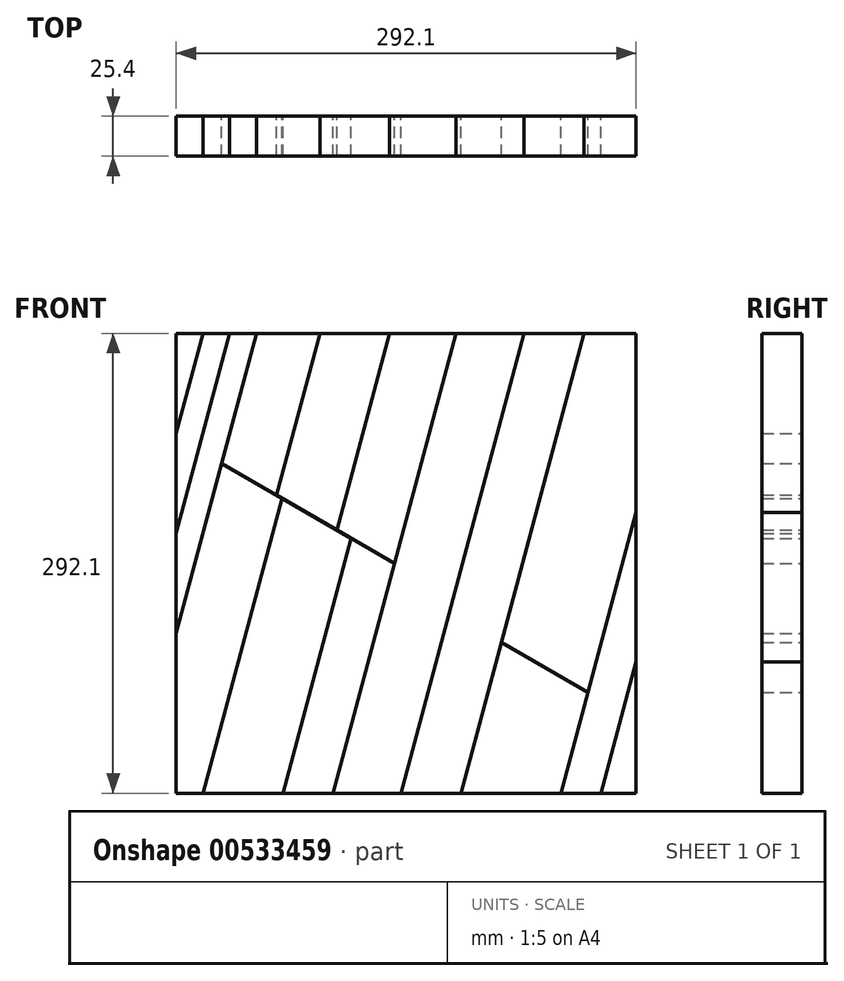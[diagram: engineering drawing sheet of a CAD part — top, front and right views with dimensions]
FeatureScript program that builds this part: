
annotation { "Feature Type Name" : "Feature", "Feature Type Description" : "" }
export const myFeature = defineFeature(function(context is Context, id is Id, definition is map)
    precondition{}
    {
        {
            var Q0;
            Q0=qCreatedBy(makeId("Front.planeOp"),FACE);
            var sketch = newSketch(context, id + "F0", { "sketchPlane" : qUnion([Q0])});
            skLineSegment(sketch, "E0.bottom", {"start": v(-146.05, -146.05) * mm, "end": v(146.05, -146.05) * mm});
            skLineSegment(sketch, "E0.top", {"start": v(-146.05, 146.05) * mm, "end": v(146.05, 146.05) * mm});
            skLineSegment(sketch, "E0.left", {"start": v(-146.05, -146.05) * mm, "end": v(-146.05, 146.05) * mm});
            skLineSegment(sketch, "E0.right", {"start": v(146.05, -146.05) * mm, "end": v(146.05, 146.05) * mm});
            skPoint(sketch, "E0.middle", {"position": v(0, 0) * mm});
            skSolve(sketch);
        }
        {
            var Q0;
            Q0=makeQuery(id+"F0.imprint","IMPRINT",FACE,{"disambiguationData":[TD([[makeQuery(id+"F0.imprint","IMPRINT",EDGE,{"derivedFrom":sQuery(id+"F0.wireOp",EDGE,"E0.bottom")}),1.0]])]});
            var sketch = newSketch(context, id + "F1", { "sketchPlane" : qUnion([Q0])});
            skLineSegment(sketch, "E1.0", {"start": v(-146.05, -146.05) * mm, "end": v(-146.05, 146.05) * mm});
            skLineSegment(sketch, "E2.0", {"start": v(-146.05, 146.05) * mm, "end": v(146.05, 146.05) * mm});
            skLineSegment(sketch, "E3.0", {"start": v(146.05, -146.05) * mm, "end": v(146.05, 146.05) * mm});
            skLineSegment(sketch, "E4.0", {"start": v(-146.05, -146.05) * mm, "end": v(146.05, -146.05) * mm});
            skLineSegment(sketch, "E5", {"start": v(-146.05, 82.55) * mm, "end": v(-129.04, 146.05) * mm});
            skLineSegment(sketch, "E6", {"start": v(-146.05, 19.05) * mm, "end": v(-112.02, 146.05) * mm});
            skLineSegment(sketch, "E7", {"start": v(-146.05, -44.45) * mm, "end": v(-95, 146.05) * mm});
            skLineSegment(sketch, "E8", {"start": v(-117.37, 63.5) * mm, "end": v(-7.38, 0) * mm});
            skLineSegment(sketch, "E9", {"start": v(31.75, 146.05) * mm, "end": v(-46.52, -146.05) * mm});
            skLineSegment(sketch, "E10", {"start": v(-129.07, -146.05) * mm, "end": v(-78.87, 41.27) * mm});
            skLineSegment(sketch, "E11", {"start": v(-78.27, -146.05) * mm, "end": v(-34.88, 15.87) * mm});
            skLineSegment(sketch, "E12", {"start": v(-3.34, -146.05) * mm, "end": v(74.93, 146.05) * mm});
            skLineSegment(sketch, "E13", {"start": v(34.76, -146.05) * mm, "end": v(113.03, 146.05) * mm});
            skLineSegment(sketch, "E14", {"start": v(98.26, -146.05) * mm, "end": v(146.05, 32.3) * mm});
            skLineSegment(sketch, "E15", {"start": v(60.4, -50.34) * mm, "end": v(115.4, -82.1) * mm});
            skPoint(sketch, "E16.orphan", {"position": v(0, 146.05) * mm});
            skLineSegment(sketch, "E17", {"start": v(123.66, -146.05) * mm, "end": v(146.05, -62.5) * mm});
            skLineSegment(sketch, "E18", {"start": v(-44.03, 21.16) * mm, "end": v(-10.57, 146.05) * mm});
            skLineSegment(sketch, "E19", {"start": v(-82.3, 43.25) * mm, "end": v(-54.75, 146.05) * mm});
            skSolve(sketch);
        }
        {
            var Q0;
            {var subQ6=sQuery(id+"F1.wireOp",EDGE,"E17");Q0=makeQuery(id+"F1.imprint","IMPRINT",FACE,{"disambiguationData":[TD([[makeQuery(id+"F1.imprint","IMPRINT",EDGE,{"derivedFrom":subQ6}),1.0]])]});}
            extrude(context, id + "F2", {"entities" : qUnion([Q0]), "depth" : 25.4 * mm, "offsetDistance" : 25.4 * mm});
        }
        {
            var Q0;
            {var subQ3=sQuery(id+"F1.wireOp",EDGE,"E17");Q0=makeQuery(id+"F1.imprint","IMPRINT",FACE,{"disambiguationData":[TD([[makeQuery(id+"F1.imprint","IMPRINT",EDGE,{"derivedFrom":subQ3}),-1.0]])]});}
            extrude(context, id + "F3", {"entities" : qUnion([Q0]), "depth" : 25.4 * mm, "offsetDistance" : 25.4 * mm});
        }
        {
            var Q0;
            {var subQ5=sQuery(id+"F1.wireOp",EDGE,"E15");Q0=makeQuery(id+"F1.imprint","IMPRINT",FACE,{"disambiguationData":[TD([[makeQuery(id+"F1.imprint","IMPRINT",EDGE,{"derivedFrom":subQ5}),-1.0]])]});}
            extrude(context, id + "F4", {"entities" : qUnion([Q0]), "depth" : 25.4 * mm, "offsetDistance" : 25.4 * mm});
        }
        {
            var Q0;
            {var subQ3=sQuery(id+"F1.wireOp",EDGE,"E15");Q0=makeQuery(id+"F1.imprint","IMPRINT",FACE,{"disambiguationData":[TD([[makeQuery(id+"F1.imprint","IMPRINT",EDGE,{"derivedFrom":subQ3}),1.0]])]});}
            extrude(context, id + "F5", {"entities" : qUnion([Q0]), "depth" : 25.4 * mm, "offsetDistance" : 25.4 * mm});
        }
        {
            var Q0;
            {var subQ4=sQuery(id+"F1.wireOp",EDGE,"E12");Q0=makeQuery(id+"F1.imprint","IMPRINT",FACE,{"disambiguationData":[TD([[makeQuery(id+"F1.imprint","IMPRINT",EDGE,{"derivedFrom":subQ4}),-1.0]])]});}
            extrude(context, id + "F6", {"entities" : qUnion([Q0]), "depth" : 25.4 * mm, "offsetDistance" : 25.4 * mm});
        }
        {
            var Q0;
            {var subQ6=sQuery(id+"F1.wireOp",EDGE,"E12");Q0=makeQuery(id+"F1.imprint","IMPRINT",FACE,{"disambiguationData":[TD([[makeQuery(id+"F1.imprint","IMPRINT",EDGE,{"derivedFrom":subQ6}),1.0]])]});}
            extrude(context, id + "F7", {"entities" : qUnion([Q0]), "depth" : 25.4 * mm, "offsetDistance" : 25.4 * mm});
        }
        {
            var Q0;
            {var subQ3=sQuery(id+"F1.wireOp",EDGE,"E11");Q0=makeQuery(id+"F1.imprint","IMPRINT",FACE,{"disambiguationData":[TD([[makeQuery(id+"F1.imprint","IMPRINT",EDGE,{"derivedFrom":subQ3}),-1.0]])]});}
            extrude(context, id + "F8", {"entities" : qUnion([Q0]), "depth" : 25.4 * mm, "offsetDistance" : 25.4 * mm});
        }
        {
            var Q0;
            {var subQ5=sQuery(id+"F1.wireOp",EDGE,"E18");Q0=makeQuery(id+"F1.imprint","IMPRINT",FACE,{"disambiguationData":[TD([[makeQuery(id+"F1.imprint","IMPRINT",EDGE,{"derivedFrom":subQ5}),-1.0]])]});}
            extrude(context, id + "F9", {"entities" : qUnion([Q0]), "depth" : 25.4 * mm, "offsetDistance" : 25.4 * mm});
        }
        {
            var Q0;
            {var subQ2=sQuery(id+"F1.wireOp",EDGE,"E18");Q0=makeQuery(id+"F1.imprint","IMPRINT",FACE,{"disambiguationData":[TD([[makeQuery(id+"F1.imprint","IMPRINT",EDGE,{"derivedFrom":subQ2}),1.0]])]});}
            extrude(context, id + "F10", {"entities" : qUnion([Q0]), "depth" : 25.4 * mm, "offsetDistance" : 25.4 * mm});
        }
        {
            var Q0;
            {var subQ3=sQuery(id+"F1.wireOp",EDGE,"E10");Q0=makeQuery(id+"F1.imprint","IMPRINT",FACE,{"disambiguationData":[TD([[makeQuery(id+"F1.imprint","IMPRINT",EDGE,{"derivedFrom":subQ3}),-1.0]])]});}
            extrude(context, id + "F11", {"entities" : qUnion([Q0]), "depth" : 25.4 * mm, "offsetDistance" : 25.4 * mm});
        }
        {
            var Q0;
            {var subQ8=sQuery(id+"F1.wireOp",EDGE,"E10");Q0=makeQuery(id+"F1.imprint","IMPRINT",FACE,{"disambiguationData":[TD([[makeQuery(id+"F1.imprint","IMPRINT",EDGE,{"derivedFrom":subQ8}),1.0]])]});}
            extrude(context, id + "F12", {"entities" : qUnion([Q0]), "depth" : 25.4 * mm, "offsetDistance" : 25.4 * mm});
        }
        {
            var Q0;
            {var subQ3=sQuery(id+"F1.wireOp",EDGE,"E19");Q0=makeQuery(id+"F1.imprint","IMPRINT",FACE,{"disambiguationData":[TD([[makeQuery(id+"F1.imprint","IMPRINT",EDGE,{"derivedFrom":subQ3}),1.0]])]});}
            extrude(context, id + "F13", {"entities" : qUnion([Q0]), "depth" : 25.4 * mm, "offsetDistance" : 25.4 * mm});
        }
        {
            var Q0;
            {var subQ0=sQuery(id+"F1.wireOp",EDGE,"E6");Q0=makeQuery(id+"F1.imprint","IMPRINT",FACE,{"disambiguationData":[TD([[makeQuery(id+"F1.imprint","IMPRINT",EDGE,{"derivedFrom":subQ0}),-1.0]])]});}
            extrude(context, id + "F14", {"entities" : qUnion([Q0]), "depth" : 25.4 * mm, "offsetDistance" : 25.4 * mm});
        }
        {
            var Q0;
            {var subQ0=sQuery(id+"F1.wireOp",EDGE,"E5");Q0=makeQuery(id+"F1.imprint","IMPRINT",FACE,{"disambiguationData":[TD([[makeQuery(id+"F1.imprint","IMPRINT",EDGE,{"derivedFrom":subQ0}),-1.0]])]});}
            extrude(context, id + "F15", {"entities" : qUnion([Q0]), "depth" : 25.4 * mm, "offsetDistance" : 25.4 * mm});
        }
        {
            var Q0;
            {var subQ3=sQuery(id+"F1.wireOp",EDGE,"E5");Q0=makeQuery(id+"F1.imprint","IMPRINT",FACE,{"disambiguationData":[TD([[makeQuery(id+"F1.imprint","IMPRINT",EDGE,{"derivedFrom":subQ3}),1.0]])]});}
            extrude(context, id + "F16", {"entities" : qUnion([Q0]), "depth" : 25.4 * mm, "offsetDistance" : 25.4 * mm});
        }
    });
